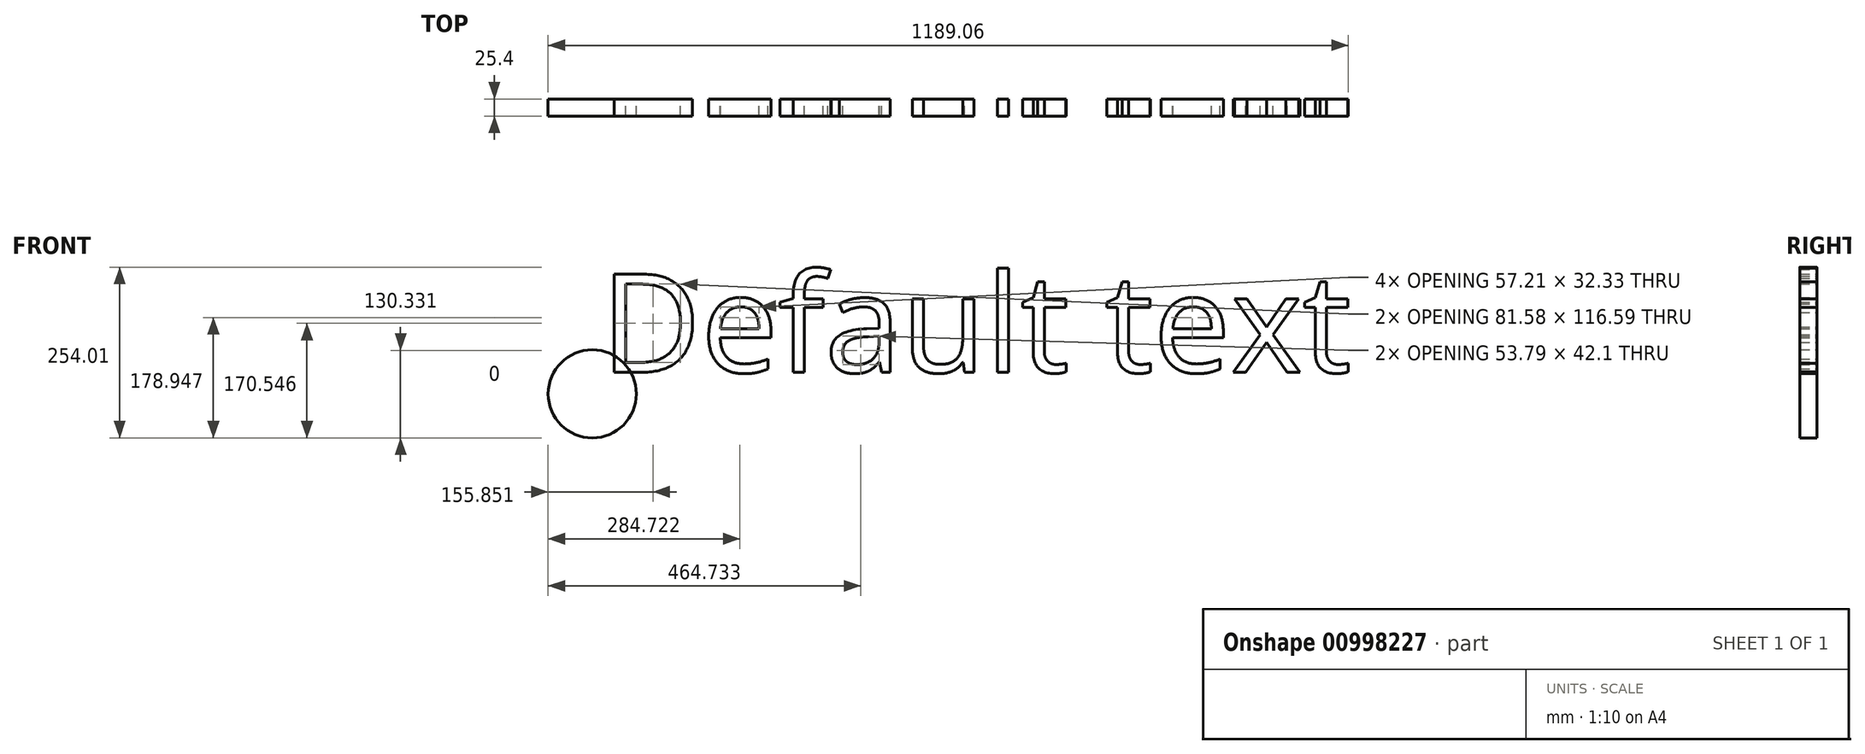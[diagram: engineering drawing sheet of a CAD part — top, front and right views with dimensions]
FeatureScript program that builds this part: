
annotation { "Feature Type Name" : "Feature", "Feature Type Description" : "" }
export const myFeature = defineFeature(function(context is Context, id is Id, definition is map)
    precondition{}
    {
        {
            var Q0;
            Q0=qCreatedBy(makeId("Front.planeOp"),FACE);
            var sketch = newSketch(context, id + "F0", { "sketchPlane" : qUnion([Q0])});
            skCircle(sketch, "E0", {"center": v(-54.22, 0) * mm, "radius": 65.56 * mm});
            skSolve(sketch);
        }
        {
            var Q0;
            Q0=qCreatedBy(makeId("Front.planeOp"),FACE);
            var sketch = newSketch(context, id + "F1", { "sketchPlane" : qUnion([Q0])});
            skText(sketch, "E1", { "text": "Default text", "fontName": "OpenSans-Regular.ttf"});
            const initialGuessF1  = {"E1": [-0.04174, 0.03203, 1, 0, 0.14719]};
            skSetInitialGuess(sketch, initialGuessF1);
            skSolve(sketch);
        }
        {
            var Q0;
            Q0 = qSketchRegion(id + "F1", true);
            var Q1;
            Q1=makeQuery(id+"F0.imprint","IMPRINT",FACE,{"disambiguationData":[TD([[makeQuery(id+"F0.imprint","IMPRINT",EDGE,{"derivedFrom":sQuery(id+"F0.wireOp",EDGE,"E0")}),1.0]])]});
            extrude(context, id + "F2", {"entities" : qUnion([Q0, Q1]), "depth" : 25.4 * mm, "offsetDistance" : 25.4 * mm});
        }
        {
            var Q0;
            Q0 = qSketchRegion(id + "F1", true);
            extrude(context, id + "F3", {"entities" : qUnion([Q0]), "depth" : 25.4 * mm, "offsetDistance" : 25.4 * mm});
        }
    });
